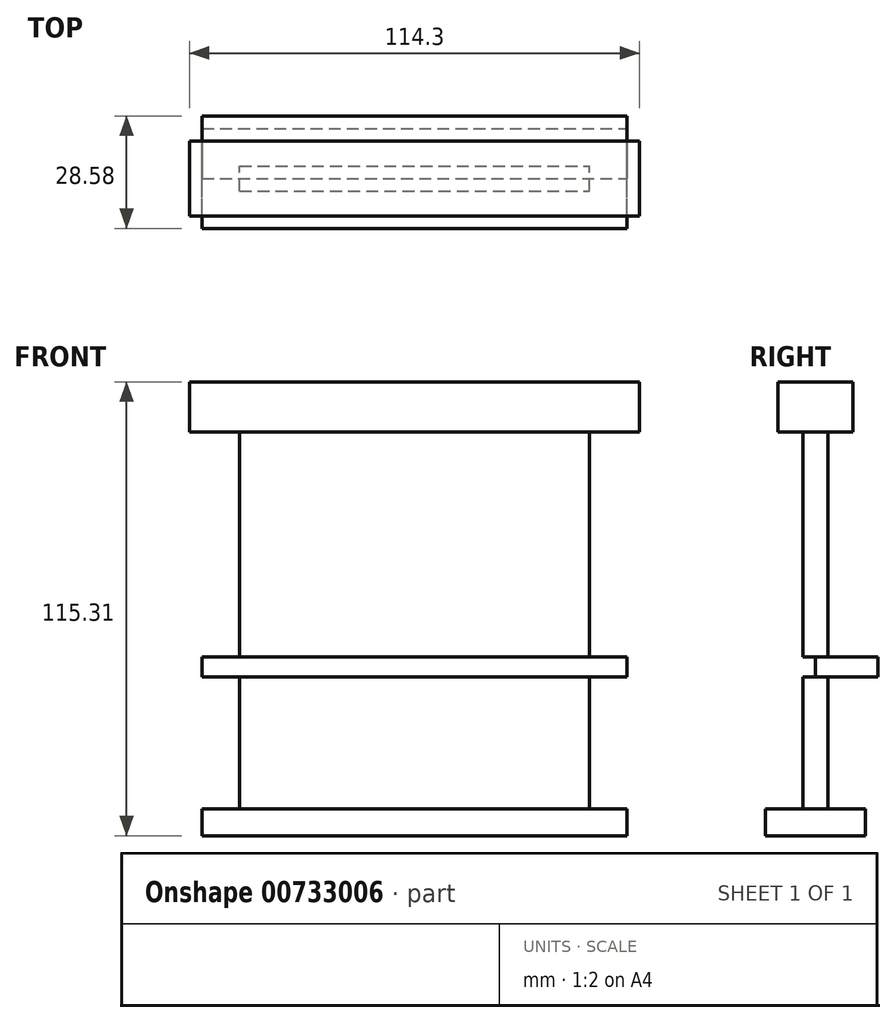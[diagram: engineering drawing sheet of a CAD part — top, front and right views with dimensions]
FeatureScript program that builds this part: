
annotation { "Feature Type Name" : "Feature", "Feature Type Description" : "" }
export const myFeature = defineFeature(function(context is Context, id is Id, definition is map)
    precondition{}
    {
        {
            var Q0;
            Q0=qCreatedBy(makeId("Front.planeOp"),FACE);
            var sketch = newSketch(context, id + "F0", { "sketchPlane" : qUnion([Q0])});
            skLineSegment(sketch, "E0", {"start": v(-47.18, 64.49) * mm, "end": v(67.12, 64.49) * mm});
            skLineSegment(sketch, "E1", {"start": v(-47.18, 64.49) * mm, "end": v(-47.18, 51.79) * mm});
            skLineSegment(sketch, "E2", {"start": v(67.12, 64.49) * mm, "end": v(67.12, 51.79) * mm});
            skLineSegment(sketch, "E3", {"start": v(-47.18, 51.79) * mm, "end": v(67.12, 51.79) * mm});
            skLineSegment(sketch, "E4", {"start": v(-47.18, 51.79) * mm, "end": v(-34.48, 51.79) * mm});
            skLineSegment(sketch, "E5", {"start": v(67.12, 51.79) * mm, "end": v(54.42, 51.79) * mm});
            skLineSegment(sketch, "E6", {"start": v(-34.48, 51.79) * mm, "end": v(-34.48, -5.36) * mm});
            skLineSegment(sketch, "E7", {"start": v(54.42, 51.79) * mm, "end": v(54.42, -5.36) * mm});
            skLineSegment(sketch, "E8", {"start": v(-34.48, -5.36) * mm, "end": v(54.42, -5.36) * mm});
            skLineSegment(sketch, "E9", {"start": v(-34.48, -5.36) * mm, "end": v(-44, -5.36) * mm});
            skLineSegment(sketch, "E10", {"start": v(54.42, -5.36) * mm, "end": v(63.94, -5.36) * mm});
            skLineSegment(sketch, "E11", {"start": v(-44, -5.36) * mm, "end": v(-44, -10.46) * mm});
            skLineSegment(sketch, "E12", {"start": v(63.94, -5.36) * mm, "end": v(63.94, -10.46) * mm});
            skLineSegment(sketch, "E13", {"start": v(-44, -10.46) * mm, "end": v(63.94, -10.46) * mm});
            skLineSegment(sketch, "E14", {"start": v(-34.48, -10.46) * mm, "end": v(-34.48, -44) * mm});
            skLineSegment(sketch, "E15", {"start": v(54.42, -10.46) * mm, "end": v(54.42, -44) * mm});
            skLineSegment(sketch, "E16", {"start": v(-34.48, -44) * mm, "end": v(54.42, -44) * mm});
            skLineSegment(sketch, "E17", {"start": v(54.42, -44) * mm, "end": v(63.94, -44) * mm});
            skLineSegment(sketch, "E18", {"start": v(63.94, -44) * mm, "end": v(63.94, -50.82) * mm});
            skLineSegment(sketch, "E19", {"start": v(-34.48, -44) * mm, "end": v(-44, -44) * mm});
            skLineSegment(sketch, "E20", {"start": v(-44, -44) * mm, "end": v(-44, -50.82) * mm});
            skLineSegment(sketch, "E21", {"start": v(-44, -50.82) * mm, "end": v(63.94, -50.82) * mm});
            skSolve(sketch);
        }
        {
            var Q0;
            Q0=makeQuery(id+"F0.imprint","IMPRINT",FACE,{"disambiguationData":[TD([[makeQuery(id+"F0.imprint","IMPRINT",EDGE,{"derivedFrom":sQuery(id+"F0.wireOp",EDGE,"E0")}),-1.0]])]});
            extrude(context, id + "F1", {"entities" : qUnion([Q0]), "endBound" : BoundingType.SYMMETRIC, "depth" : 19.05 * mm, "offsetDistance" : 25.4 * mm});
        }
        {
            var Q0;
            Q0=makeQuery(id+"F0.imprint","IMPRINT",FACE,{"disambiguationData":[TD([[makeQuery(id+"F0.imprint","IMPRINT",EDGE,{"derivedFrom":sQuery(id+"F0.wireOp",EDGE,"E3")}),-1.0]])]});
            var Q1;
            {var subQ0=sQuery(id+"F0.wireOp",EDGE,"E14");Q1=makeQuery(id+"F0.imprint","IMPRINT",FACE,{"disambiguationData":[TD([[makeQuery(id+"F0.imprint","IMPRINT",EDGE,{"derivedFrom":subQ0}),1.0]])]});}
            extrude(context, id + "F2", {"entities" : qUnion([Q0, Q1]), "operationType" : NewBodyOperationType.ADD, "endBound" : BoundingType.SYMMETRIC, "depth" : 6.35 * mm, "offsetDistance" : 25.4 * mm});
        }
        {
            var Q0;
            Q0=makeQuery(id+"F0.imprint","IMPRINT",FACE,{"disambiguationData":[TD([[makeQuery(id+"F0.imprint","IMPRINT",EDGE,{"derivedFrom":sQuery(id+"F0.wireOp",EDGE,"E16")}),-1.0]])]});
            extrude(context, id + "F3", {"entities" : qUnion([Q0]), "endBound" : BoundingType.SYMMETRIC, "depth" : 25.4 * mm, "offsetDistance" : 25.4 * mm});
        }
        {
            var Q0;
            Q0=makeQuery(id+"F0.imprint","IMPRINT",FACE,{"disambiguationData":[TD([[makeQuery(id+"F0.imprint","IMPRINT",EDGE,{"derivedFrom":sQuery(id+"F0.wireOp",EDGE,"E8")}),-1.0]])]});
            extrude(context, id + "F4", {"entities" : qUnion([Q0]), "oppositeDirection" : true, "depth" : 15.88 * mm, "offsetDistance" : 25.4 * mm});
        }
    });
